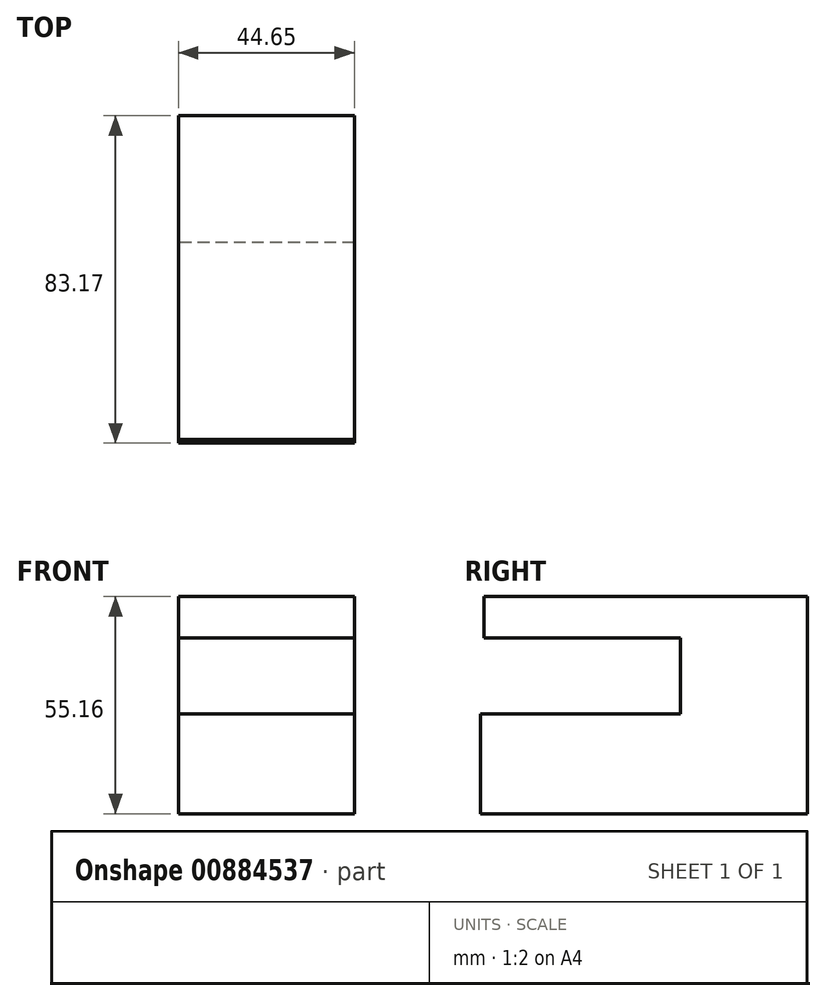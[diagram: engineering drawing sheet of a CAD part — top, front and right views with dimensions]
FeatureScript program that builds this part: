
annotation { "Feature Type Name" : "Feature", "Feature Type Description" : "" }
export const myFeature = defineFeature(function(context is Context, id is Id, definition is map)
    precondition{}
    {
        {
            var Q0;
            Q0=qCreatedBy(makeId("Top.planeOp"),FACE);
            var sketch = newSketch(context, id + "F0", { "sketchPlane" : qUnion([Q0])});
            skLineSegment(sketch, "E0.bottom", {"start": v(-61.46, 83.17) * mm, "end": v(-16.81, 83.17) * mm});
            skLineSegment(sketch, "E0.top", {"start": v(-61.46, 0) * mm, "end": v(-16.81, 0) * mm});
            skLineSegment(sketch, "E0.left", {"start": v(-61.46, 83.17) * mm, "end": v(-61.46, 0) * mm});
            skLineSegment(sketch, "E0.right", {"start": v(-16.81, 83.17) * mm, "end": v(-16.81, 0) * mm});
            skSolve(sketch);
        }
        {
            var Q0;
            Q0=makeQuery(id+"F0.imprint","IMPRINT",FACE,{"disambiguationData":[TD([[makeQuery(id+"F0.imprint","IMPRINT",EDGE,{"derivedFrom":sQuery(id+"F0.wireOp",EDGE,"E0.bottom")}),-1.0]])]});
            extrude(context, id + "F1", {"entities" : qUnion([Q0]), "depth" : 25.4 * mm, "offsetDistance" : 25.4 * mm});
        }
        {
            var Q0;
            Q0=makeQuery(id+"F1.opExtrude","CAP_FACE",FACE,{"disambiguationData":[OSD([sQuery(id+"F0.wireOp",EDGE,"E0.bottom"),sQuery(id+"F0.wireOp",EDGE,"E0.top"),sQuery(id+"F0.wireOp",EDGE,"E0.left"),sQuery(id+"F0.wireOp",EDGE,"E0.right")])],"isStart":false});
            var sketch = newSketch(context, id + "F2", { "sketchPlane" : qUnion([Q0])});
            skLineSegment(sketch, "E1", {"start": v(-16.81, 50.9) * mm, "end": v(-61.46, 50.9) * mm});
            skSolve(sketch);
        }
        {
            var Q0;
            {var subQ0=sQuery(id+"F2.wireOp",EDGE,"E1");Q0=makeQuery(id+"F2.imprint","IMPRINT",FACE,{"disambiguationData":[TD([[makeQuery(id+"F2.imprint","IMPRINT",EDGE,{"derivedFrom":subQ0}),-1.0]])]});}
            extrude(context, id + "F3", {"entities" : qUnion([Q0]), "operationType" : NewBodyOperationType.ADD, "depth" : 29.76 * mm, "offsetDistance" : 25.4 * mm});
        }
        {
            var Q0;
            Q0=makeQuery(id+"F3.opExtrude","SWEPT_FACE",FACE,{"disambiguationData":[OSD([sQuery(id+"F2.wireOp",EDGE,"E1")])]});
            var sketch = newSketch(context, id + "F4", { "sketchPlane" : qUnion([Q0])});
            skLineSegment(sketch, "E2", {"start": v(-61.46, 44.64) * mm, "end": v(-16.81, 44.64) * mm});
            skSolve(sketch);
        }
        {
            var Q0;
            {var subQ0=sQuery(id+"F4.wireOp",EDGE,"E2");Q0=makeQuery(id+"F4.imprint","IMPRINT",FACE,{"disambiguationData":[TD([[makeQuery(id+"F4.imprint","IMPRINT",EDGE,{"derivedFrom":subQ0}),1.0]])]});}
            extrude(context, id + "F5", {"entities" : qUnion([Q0]), "operationType" : NewBodyOperationType.ADD, "depth" : 49.92 * mm, "offsetDistance" : 25.4 * mm});
        }
    });
